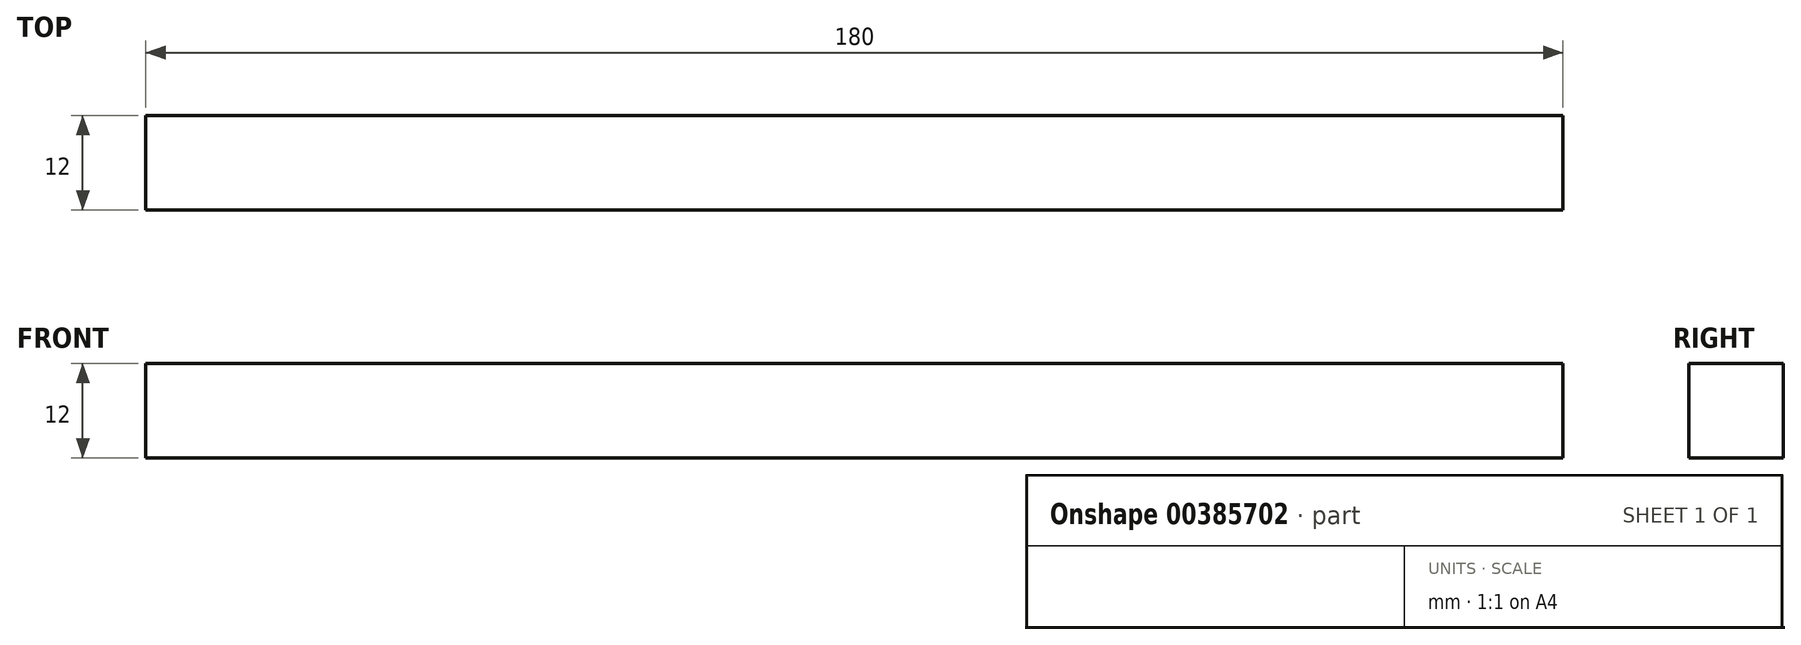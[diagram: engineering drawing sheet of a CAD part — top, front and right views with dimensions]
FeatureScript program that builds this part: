
annotation { "Feature Type Name" : "Feature", "Feature Type Description" : "" }
export const myFeature = defineFeature(function(context is Context, id is Id, definition is map)
    precondition{}
    {
        {
            var Q0;
            Q0=qCreatedBy(makeId("Front.planeOp"),FACE);
            var sketch = newSketch(context, id + "F0", { "sketchPlane" : qUnion([Q0])});
            skLineSegment(sketch, "E0.bottom", {"start": v(90, -6) * mm, "end": v(-90, -6) * mm});
            skLineSegment(sketch, "E0.top", {"start": v(90, 6) * mm, "end": v(-90, 6) * mm});
            skLineSegment(sketch, "E0.left", {"start": v(90, -6) * mm, "end": v(90, 6) * mm});
            skLineSegment(sketch, "E0.right", {"start": v(-90, -6) * mm, "end": v(-90, 6) * mm});
            skPoint(sketch, "E0.middle", {"position": v(0, 0) * mm});
            skSolve(sketch);
        }
        {
            var Q0;
            Q0=makeQuery(id+"F0.imprint","IMPRINT",FACE,{"disambiguationData":[TD([[makeQuery(id+"F0.imprint","IMPRINT",EDGE,{"derivedFrom":sQuery(id+"F0.wireOp",EDGE,"E0.bottom")}),-1.0]])]});
            extrude(context, id + "F1", {"entities" : qUnion([Q0]), "depth" : 12 * mm});
        }
    });
